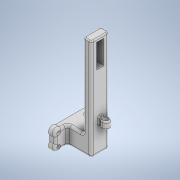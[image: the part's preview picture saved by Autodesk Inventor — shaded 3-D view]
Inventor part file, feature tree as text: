
AUTODESK INVENTOR PART (.ipt)
format: ipt  version: 2021 (Build 250183000, 183)  size: 330,240 bytes
history: native  units: mm
features: sketch x8, extrude x7, fillet x4, other x1
ambient origin geometry x8: Origin, YZ Plane, XZ Plane, XY Plane, X Axis, Y Axis, Z Axis, Center Point
bodies: Body1 (feature_tree)
feature tree (20):
  other  "Sólido1"
  sketch  "Boceto1"  dims[d11=5.0mm d12=0.0mm d15=20.0mm d16=0.0mm]
  extrude  "Extrusión1"  Depth=20.0mm TaperAngle=0.0deg
  extrude  "Extrusión2"  Depth=2.0mm
  extrude  "Extrusión3"  Depth=10.0mm TaperAngle=0.0deg
  fillet  "Empalme1"  Radius=1.0mm
  fillet  "Empalme2"  Radius=10.0mm
  extrude  "Extrusión4"  Depth=4.0mm
  fillet  "Empalme3"  Radius=1.5mm
  extrude  "Extrusión5"  Depth=3.0mm
  extrude  "Extrusión6"  Depth=10.0mm TaperAngle=0.0deg
  extrude  "Extrusión7"  Depth=1.0mm
  fillet  "Empalme4"  Radius=0.872665mm
  sketch  "Boceto2"  dims[d18=70.0mm d19=0.0mm d20=2.0mm]
  sketch  "Boceto3"  dims[d21=2.0mm d27=70.0mm d28=0.0mm d29=1.0mm d35=10.0mm d36=0.0mm]
  sketch  "Boceto4"  dims[d37=10.0mm d38=0.0mm d39=4.0mm d40=1.5mm]
  sketch  "Boceto5"  dims[d41=1.5mm d42=3.0mm]
  sketch  "Boceto6"  dims[d43=3.0mm d44=10.0mm d45=0.0mm]
  sketch  "Boceto7"  dims[d46=1.0mm d2=0.5mm d3=0.872665mm]
  sketch  "Boceto8"  dims[d4=0.5mm d5=0.872665mm d13=0.5mm d14=0.872665mm]
